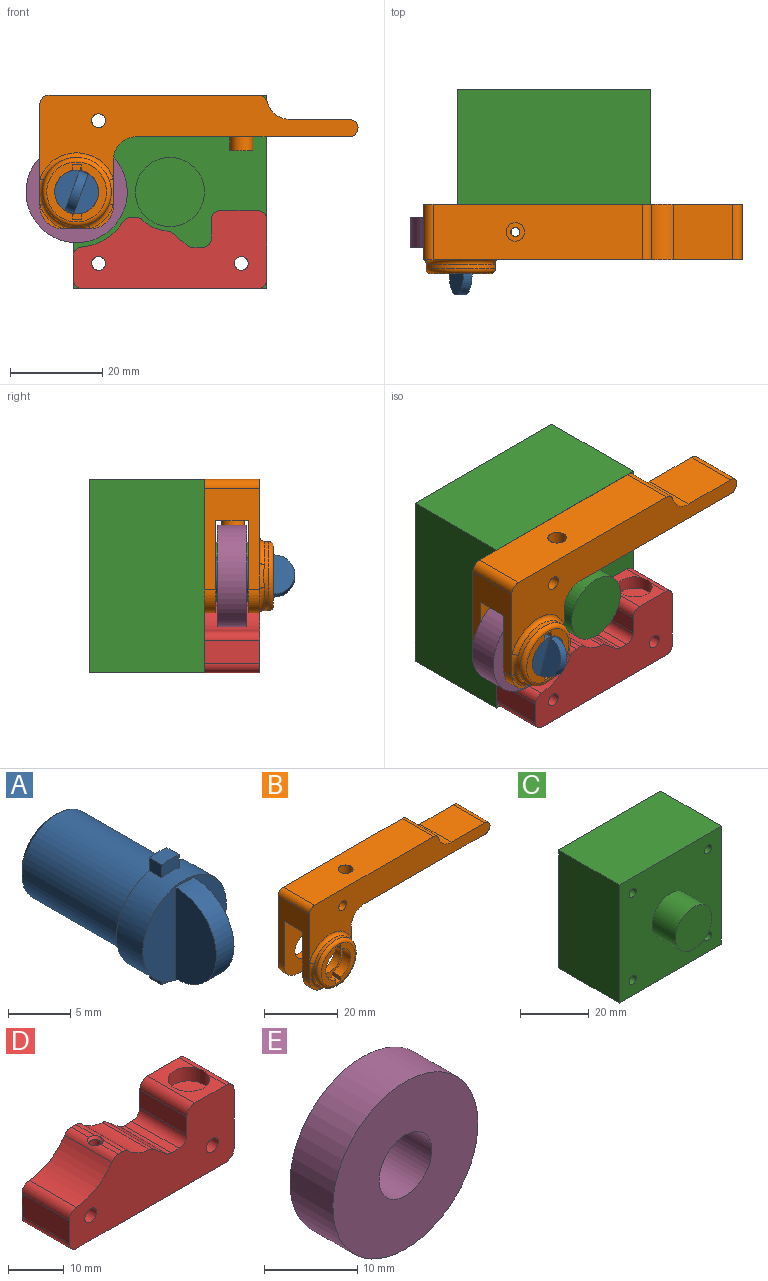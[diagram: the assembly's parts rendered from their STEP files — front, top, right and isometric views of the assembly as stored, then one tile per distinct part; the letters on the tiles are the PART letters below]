
ASSEMBLY  parts=5 mates=4
PART A: 17 faces, bbox 9.5x19.6x12 mm
  f0: cylinder r=4mm len=11.5mm, axis (0,1,0), area 289mm2, adj f6,f13
  f1: plane 7x7mm, normal (0,1,0), area 38.5mm2, adj f13
  f2: cylinder r=6mm len=2mm, axis (0,1,0), area 2.8mm2, adj f3,f4,f5,f6
  f3: plane 1.4x1.27mm, normal (-1,0,0), area 1.8mm2, adj f2,f5,f6,f11
  f4: plane 1.4x1.27mm, normal (1,0,0), area 1.8mm2, adj f2,f5,f6,f11
  f5: plane 2x1.36mm, normal (0,-1,0), area 2.5mm2, adj f2,f3,f4,f11
  f6: plane 12x9.5mm, normal (0,1,0), area 25.6mm2, adj f0,f2,f3,f4,f7,f8,f9,f11
  f7: plane 1.4x1.27mm, normal (-1,0,0), area 1.8mm2, adj f6,f8,f10,f11
  f8: cylinder r=6mm len=2mm, axis (0,1,0), area 2.8mm2, adj f6,f7,f9,f10
  f9: plane 1.4x1.27mm, normal (1,0,0), area 1.8mm2, adj f6,f8,f10,f11
  f10: plane 2x1.36mm, normal (0,-1,0), area 2.5mm2, adj f7,f8,f9,f11
  f11: cylinder r=4.75mm len=9.5mm, axis (0,1,0), area 83.9mm2, adj f3,f4,f5,f6,f7,f9,f10,f12
  f12: plane 9.5x9.5mm, normal (0,-1,0), area 52.9mm2, adj f11,f14,f15,f16
  f13: cone r=4mm half-angle=45deg, axis (0,-1,0), area 16.7mm2, adj f0,f1
  f14: cylinder r=4.5mm len=9mm, axis (-1,0,0), area 28.8mm2, adj f12,f15,f16
  f15: plane 9x4.63mm, normal (1,0,0), area 33mm2, adj f12,f14
  f16: plane 9x4.63mm, normal (-1,0,0), area 33mm2, adj f12,f14
PART B: 56 faces, bbox 70.5x15x30.4 mm
  f0: plane 5.13x5.13mm, normal (0,-1,0), area 3.8mm2, adj f10,f18,f20,f53
  f1: plane 69.09x18.13mm, normal (0,-1,0), area 599.1mm2, adj f7,f12,f13,f14,f15,f16,f17,f18
  f2: plane 12x9.78mm, normal (0,-1,0), area 36.2mm2, adj f19,f35,f36,f37,f38,f39,f40,f41
  f3: plane 6x2.45mm, normal (0,0,-1), area 14.7mm2, adj f5,f9,f23,f30
  f4: cylinder r=1mm len=4.04mm, axis (0,0,1), area 25.2mm2, adj f7,f25,f26,f27,f28
  f5: cylinder r=5mm len=5mm, axis (0,1,0), area 19.2mm2, adj f3,f6,f23,f30
  f6: plane 10x2.45mm, normal (1,0,0), area 24.5mm2, adj f5,f7,f23,f30
  f7: cylinder r=5mm len=12mm, axis (0,1,0), area 42.8mm2, adj f1,f4,f6,f12,f13,f23,f26,f27
  f8: cylinder r=4mm len=8mm, axis (0,1,0), area 61.6mm2, adj f23,f30
  f9: cylinder r=5mm len=5mm, axis (0,1,0), area 19.2mm2, adj f3,f18,f23,f30
  f10: plane 6.04x2.49mm, normal (0,0,-1), area 14.7mm2, adj f0,f11,f20,f22,f29,f55
  f11: cylinder r=5mm len=5mm, axis (0,1,0), area 19.2mm2, adj f10,f12,f22,f29
  f12: plane 10.04x2.49mm, normal (1,0,0), area 24.5mm2, adj f1,f7,f11,f22,f29,f52
  f13: plane 46.2x12mm, normal (0,0,-1), area 534.8mm2, adj f1,f7,f14,f23,f33
  f14: cylinder r=1.88mm len=12mm, axis (0,1,0), area 72.7mm2, adj f1,f13,f15,f23
  f15: plane 12.82x12mm, normal (0,0,1), area 153.8mm2, adj f1,f14,f16,f23
  f16: cylinder r=5mm len=12mm, axis (0,1,0), area 79mm2, adj f1,f15,f23,f31
  f17: plane 45.48x12mm, normal (0,0,1), area 533.1mm2, adj f1,f23,f24,f31,f32
  f18: plane 22.04x12.04mm, normal (-1,0,0), area 157.5mm2, adj f0,f1,f9,f20,f23,f28,f29,f30
  f19: cylinder r=4mm len=8mm, axis (0,1,0), area 61.6mm2, adj f2,f29
  f20: cylinder r=5mm len=5mm, axis (0,1,0), area 19.2mm2, adj f0,f10,f18,f29
  f21: cylinder r=1.5mm len=12mm, axis (0,1,0), area 113.1mm2, adj f1,f23
  f22: plane 5.13x5.13mm, normal (0,-1,0), area 3.8mm2, adj f10,f11,f12,f54
  f23: plane 69.09x29mm, normal (0,1,0), area 777.6mm2, adj f3,f5,f6,f7,f8,f9,f13,f14
  f24: cylinder r=2mm len=5mm, axis (0,0,1), area 62.8mm2, adj f17,f25
  f25: plane 4x4mm, normal (0,0,1), area 9.4mm2, adj f4,f24
  f26: plane 2.66x0.04mm, normal (-1,0,0), area 0.1mm2, adj f4,f7,f28,f29
  f27: plane 2.66x0.04mm, normal (-1,0,0), area 0.1mm2, adj f4,f7,f28,f30
  f28: plane 20.33x7.1mm, normal (0,0,-1), area 141.9mm2, adj f4,f18,f26,f27,f29,f30
  f29: plane 20.33x20mm, normal (0,1,0), area 264.4mm2, adj f7,f10,f11,f12,f18,f19,f20,f26
  f30: plane 20.33x20mm, normal (0,-1,0), area 264.4mm2, adj f3,f5,f6,f7,f8,f9,f18,f27
  f31: cylinder r=2mm len=12mm, axis (0,1,0), area 31.6mm2, adj f1,f16,f17,f23
  f32: cylinder r=2mm len=12mm, axis (0,1,0), area 37.7mm2, adj f1,f17,f18,f23
  f33: cylinder r=2.5mm len=5mm, axis (0,0,1), area 47.1mm2, adj f13,f34
  f34: plane 5x5mm, normal (0,0,-1), area 19.6mm2, adj f33
  f35: cylinder r=6mm len=5.89mm, axis (0,1,0), area 13.1mm2, adj f2,f36,f42,f44,f45,f47
  f36: plane 1.5x0.9mm, normal (0.71,0,-0.71), area 1.9mm2, adj f2,f35,f37,f44
  f37: cylinder r=4.75mm len=9.29mm, axis (0,1,0), area 33.1mm2, adj f2,f36,f38,f44,f45,f47
  f38: plane 3x1.27mm, normal (1,0,0), area 3.8mm2, adj f2,f37,f39,f47
  f39: cylinder r=6mm len=5.89mm, axis (0,1,0), area 13.1mm2, adj f2,f38,f40,f46,f47,f48
  f40: plane 1.5x0.9mm, normal (-0.71,0,0.71), area 1.9mm2, adj f2,f39,f41,f48
  f41: cylinder r=4.75mm len=9.29mm, axis (0,1,0), area 33.1mm2, adj f2,f40,f42,f46,f47,f48
  f42: plane 3x1.27mm, normal (-1,0,0), area 3.8mm2, adj f2,f35,f41,f47
  f43: cylinder r=7.5mm len=15mm, axis (0,1,0), area 47.1mm2, adj f49,f50,f51,f52,f53,f54,f55
  f44: plane 3.89x3.34mm, normal (0,1,0), area 5.3mm2, adj f35,f36,f37,f45
  f45: plane 1.5x1.27mm, normal (1,0,0), area 1.9mm2, adj f35,f37,f44,f47
  f46: plane 1.5x1.27mm, normal (-1,0,0), area 1.9mm2, adj f39,f41,f47,f48
  f47: plane 13x13mm, normal (0,-1,0), area 56.8mm2, adj f35,f37,f38,f39,f41,f42,f45,f46
  f48: plane 3.89x3.34mm, normal (0,1,0), area 5.3mm2, adj f39,f40,f41,f46
  f49: torus R=6.5mm, axis (0,-1,0), area 70.4mm2, adj f43,f47
  f50: torus R=8.5mm, axis (0,-1,0), area 30.3mm2, adj f1,f43,f51,f52
  f51: bspline ~6.25x1.14mm, area 6.5mm2, adj f18,f43,f50,f53
  f52: bspline ~6.25x1.14mm, area 6.5mm2, adj f12,f43,f50,f54
  f53: torus R=8.5mm, axis (0,-1,0), area 10.9mm2, adj f0,f43,f51,f55
  f54: torus R=8.5mm, axis (0,-1,0), area 10.9mm2, adj f22,f43,f52,f55
  f55: bspline ~6.25x1.14mm, area 6.5mm2, adj f10,f43,f53,f54
PART C: 12 faces, bbox 42x34.6x42 mm
  f0: plane 42x25mm, normal (0,0,1), area 1050mm2, adj f1,f7,f8,f9
  f1: plane 42x25mm, normal (-1,0,0), area 1050mm2, adj f0,f2,f8,f9
  f2: plane 42x25mm, normal (0,0,-1), area 1050mm2, adj f1,f7,f8,f9
  f3: cylinder r=1.5mm len=25mm, axis (0,-1,0), area 235.6mm2, adj f8,f9
  f4: cylinder r=1.5mm len=25mm, axis (0,-1,0), area 235.6mm2, adj f8,f9
  f5: cylinder r=1.5mm len=25mm, axis (0,-1,0), area 235.6mm2, adj f8,f9
  f6: cylinder r=1.5mm len=25mm, axis (0,-1,0), area 235.6mm2, adj f8,f9
  f7: plane 42x25mm, normal (1,0,0), area 1050mm2, adj f0,f2,f8,f9
  f8: plane 42x42mm, normal (0,1,0), area 1735.7mm2, adj f0,f1,f2,f3,f4,f5,f6,f7
  f9: plane 42x42mm, normal (0,-1,0), area 1559mm2, adj f0,f1,f2,f3,f4,f5,f6,f7
  f10: cylinder r=7.5mm len=15mm, axis (0,1,0), area 452.4mm2, adj f9,f11
  f11: plane 15x15mm, normal (0,-1,0), area 176.7mm2, adj f10
PART D: 37 faces, bbox 42x12x17 mm
  f0: plane 4.97x1.18mm, normal (0,0,1), area 5.5mm2, adj f13,f26,f27,f30
  f1: cylinder r=12mm len=12mm, axis (0,1,0), area 131.2mm2, adj f13,f14,f27,f34
  f2: plane 12x5.06mm, normal (-1,0,0), area 60.7mm2, adj f13,f14,f34,f35
  f3: plane 38x12mm, normal (0,0,-1), area 405.7mm2, adj f13,f14,f19,f35,f36
  f4: plane 13x12mm, normal (1,0,0), area 156mm2, adj f13,f14,f32,f36
  f5: plane 12x8mm, normal (0,0,1), area 52.3mm2, adj f13,f14,f15,f32,f33
  f6: plane 12x4mm, normal (-1,0,0), area 48mm2, adj f13,f14,f31,f33
  f7: plane 12x2mm, normal (0,0,1), area 24mm2, adj f13,f14,f28,f31
  f8: plane 12x3.22mm, normal (0.63,0,0.77), area 49.8mm2, adj f13,f14,f28,f29
  f9: cylinder r=8.5mm len=12mm, axis (0,1,0), area 71mm2, adj f13,f14,f29,f30
  f10: cylinder r=1.5mm len=12mm, axis (0,1,0), area 113.1mm2, adj f13,f14
  f11: plane 4.97x1.18mm, normal (0,0,1), area 5.5mm2, adj f14,f26,f27,f30
  f12: cylinder r=1.5mm len=12mm, axis (0,1,0), area 113.1mm2, adj f13,f14
  f13: plane 42x17mm, normal (0,-1,0), area 532.2mm2, adj f0,f1,f2,f3,f4,f5,f6,f7
  f14: plane 42x17mm, normal (0,1,0), area 532.2mm2, adj f1,f2,f3,f4,f5,f6,f7,f8
  f15: cylinder r=3.75mm len=7.5mm, axis (0,0,1), area 70.7mm2, adj f5,f16,f32
  f16: plane 7.5x7.5mm, normal (0,0,1), area 44.2mm2, adj f15
  f17: cylinder r=2.45mm len=5mm, axis (0,0,-1), area 26mm2, adj f20,f21,f22,f23,f24
  f18: plane 8.01x8.01mm, normal (0,0,-1), area 22.8mm2, adj f19,f21,f23,f24
  f19: cylinder r=4mm len=8mm, axis (0,0,-1), area 50.3mm2, adj f3,f18
  f20: cone r=0mm half-angle=59deg, axis (0,0,-1), area 18.3mm2, adj f17,f25
  f21: cone r=2.45mm half-angle=45deg, axis (0,0,-1), area 7mm2, adj f17,f18,f23,f24
  f22: plane 0.71x0.62mm, normal (0,-1,0), area 0.2mm2, adj f17,f23,f24
  f23: bspline ~7.08x6.13mm, area 63.3mm2, adj f17,f18,f21,f22,f24
  f24: bspline ~7.08x6.13mm, area 59mm2, adj f17,f18,f21,f22,f23
  f25: cylinder r=1mm len=6.57mm, axis (0,0,1), area 41.3mm2, adj f20,f26
  f26: cone r=1mm half-angle=45deg, axis (0,0,1), area 4.5mm2, adj f0,f11,f25,f27,f30
  f27: cylinder r=2mm len=12mm, axis (0,1,0), area 21.4mm2, adj f0,f1,f11,f13,f14,f26
  f28: cylinder r=2mm len=12mm, axis (0,-1,0), area 16.4mm2, adj f7,f8,f13,f14
  f29: cylinder r=2mm len=12mm, axis (0,1,0), area 14.7mm2, adj f8,f9,f13,f14
  f30: cylinder r=2mm len=12mm, axis (0,1,0), area 18mm2, adj f0,f9,f11,f13,f14,f26
  f31: cylinder r=2mm len=12mm, axis (0,-1,0), area 37.7mm2, adj f6,f7,f13,f14
  f32: cylinder r=2mm len=12mm, axis (0,1,0), area 37.4mm2, adj f4,f5,f13,f14,f15
  f33: cylinder r=2mm len=12mm, axis (0,-1,0), area 37.7mm2, adj f5,f6,f13,f14
  f34: cylinder r=2mm len=12mm, axis (0,1,0), area 35.6mm2, adj f1,f2,f13,f14
  f35: cylinder r=2mm len=12mm, axis (0,-1,0), area 37.7mm2, adj f2,f3,f13,f14
  f36: cylinder r=2mm len=12mm, axis (0,1,0), area 37.7mm2, adj f3,f4,f13,f14
PART E: 4 faces, bbox 22x6.5x22 mm
  f0: cylinder r=4mm len=8mm, axis (0,1,0), area 163.4mm2, adj f2,f3
  f1: cylinder r=11mm len=22mm, axis (0,1,0), area 449.2mm2, adj f2,f3
  f2: plane 22x22mm, normal (0,-1,0), area 329.9mm2, adj f0,f1
  f3: plane 22x22mm, normal (0,1,0), area 329.9mm2, adj f0,f1
PLACE A rot(axis=(0,1,0),20deg) t=(-93.25,-21.77,-54.24)mm
PLACE B t=(-81.37,-27.77,-42.24)mm
PLACE C t=(-73,-21.77,-54.24)mm fixed
PLACE D t=(-81.37,-27.77,-75.24)mm
PLACE E t=(-93.25,-27.77,-54.24)mm
MATE revolute A.f0 <-> B.f8  axis (0,1,0) through (-93.25,-33.77,-54.24)mm
MATE planar C.f4 <-> D.f10  axis (0,-1,0) through (-88.5,-21.77,-69.74)mm
MATE revolute A.f0 <-> E.f0  axis (0,1,0) through (-93.25,-28.02,-54.24)mm
MATE revolute B.f21 <-> C.f3  axis (0,1,0) through (-88.5,-21.77,-38.74)mm
